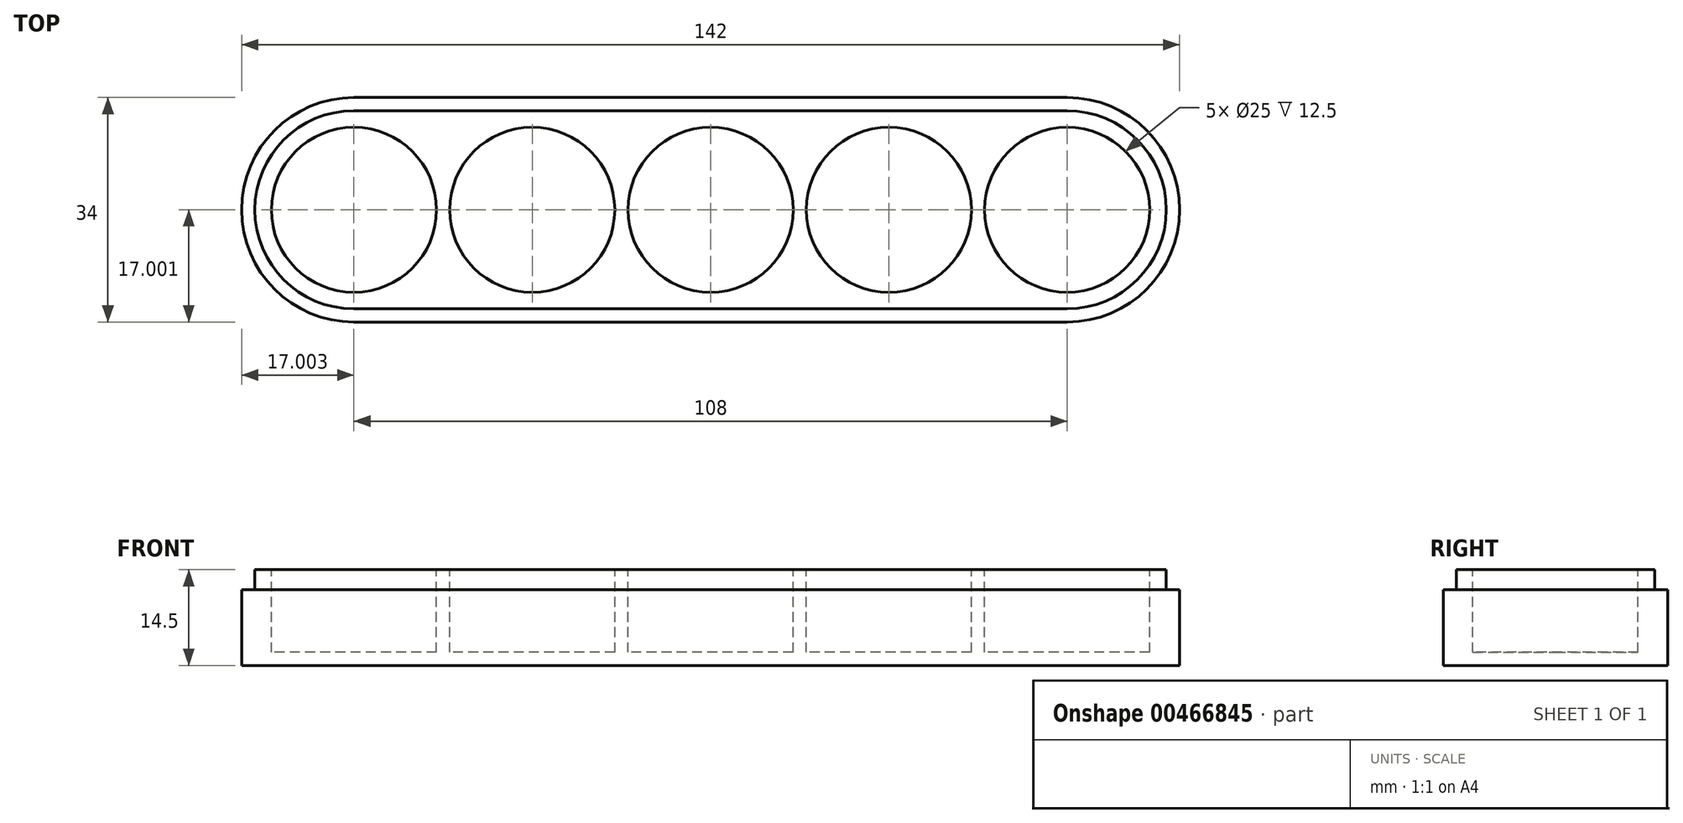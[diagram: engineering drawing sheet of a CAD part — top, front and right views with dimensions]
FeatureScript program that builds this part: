
annotation { "Feature Type Name" : "Feature", "Feature Type Description" : "" }
export const myFeature = defineFeature(function(context is Context, id is Id, definition is map)
    precondition{}
    {
        {
            var Q0;
            Q0=qCreatedBy(makeId("Top.planeOp"),FACE);
            var sketch = newSketch(context, id + "F0", { "sketchPlane" : qUnion([Q0])});
            skLineSegment(sketch, "E0.bottom", {"start": v(-55.97, 18.36) * mm, "end": v(52.03, 18.36) * mm});
            skLineSegment(sketch, "E0.top", {"start": v(-55.97, -15.64) * mm, "end": v(52.03, -15.64) * mm});
            skArc(sketch, "E1", {"start": v(-55.97, 18.36) * mm, "mid": v(-72.97, 1.36) * mm, "end": v(-55.97, -15.64) * mm});
            skArc(sketch, "E2", {"start": v(52.03, -15.64) * mm, "mid": v(69.03, 1.36) * mm, "end": v(52.03, 18.36) * mm});
            skSolve(sketch);
        }
        {
            var Q0;
            Q0=makeQuery(id+"F0.imprint","IMPRINT",FACE,{"disambiguationData":[TD([[makeQuery(id+"F0.imprint","IMPRINT",EDGE,{"derivedFrom":sQuery(id+"F0.wireOp",EDGE,"E0.bottom")}),-1.0]])]});
            extrude(context, id + "F1", {"entities" : qUnion([Q0]), "depth" : 11.5 * mm});
        }
        {
            var Q0;
            Q0=makeQuery(id+"F1.opExtrude","CAP_FACE",FACE,{"disambiguationData":[OSD([sQuery(id+"F0.wireOp",EDGE,"E0.bottom"),sQuery(id+"F0.wireOp",EDGE,"E0.top"),sQuery(id+"F0.wireOp",EDGE,"E1"),sQuery(id+"F0.wireOp",EDGE,"E2")])],"isStart":false});
            var sketch = newSketch(context, id + "F2", { "sketchPlane" : qUnion([Q0])});
            skArc(sketch, "E3.0.0", {"start": v(-55.97, 18.36) * mm, "mid": v(-72.97, 1.36) * mm, "end": v(-55.97, -15.64) * mm, "construction": true});
            skLineSegment(sketch, "E3.0.1", {"start": v(-55.97, -15.64) * mm, "end": v(52.03, -15.64) * mm, "construction": true});
            skArc(sketch, "E3.0.2", {"start": v(52.03, -15.64) * mm, "mid": v(69.03, 1.36) * mm, "end": v(52.03, 18.36) * mm, "construction": true});
            skLineSegment(sketch, "E3.0.3", {"start": v(52.03, 18.36) * mm, "end": v(-55.97, 18.36) * mm, "construction": true});
            skLineSegment(sketch, "E4.0", {"start": v(52.03, 16.36) * mm, "end": v(-55.97, 16.36) * mm});
            skArc(sketch, "E4.1", {"start": v(52.03, -13.64) * mm, "mid": v(67.03, 1.36) * mm, "end": v(52.03, 16.36) * mm});
            skLineSegment(sketch, "E4.2", {"start": v(-55.97, -13.64) * mm, "end": v(52.03, -13.64) * mm});
            skArc(sketch, "E4.3", {"start": v(-55.97, 16.36) * mm, "mid": v(-70.97, 1.36) * mm, "end": v(-55.97, -13.64) * mm});
            skSolve(sketch);
        }
        {
            var Q0;
            Q0=makeQuery(id+"F2.imprint","IMPRINT",FACE,{"disambiguationData":[TD([[makeQuery(id+"F2.imprint","IMPRINT",EDGE,{"derivedFrom":sQuery(id+"F2.wireOp",EDGE,"E4.0")}),1.0]])]});
            extrude(context, id + "F3", {"entities" : qUnion([Q0]), "operationType" : NewBodyOperationType.ADD, "depth" : 3 * mm});
        }
        {
            var Q0;
            Q0=makeQuery(id+"F3.opExtrude","CAP_FACE",FACE,{"disambiguationData":[OSD([sQuery(id+"F2.wireOp",EDGE,"E4.0"),sQuery(id+"F2.wireOp",EDGE,"E4.1"),sQuery(id+"F2.wireOp",EDGE,"E4.2"),sQuery(id+"F2.wireOp",EDGE,"E4.3")])],"isStart":false});
            var sketch = newSketch(context, id + "F4", { "sketchPlane" : qUnion([Q0])});
            skLineSegment(sketch, "E5", {"start": v(-55.97, 16.36) * mm, "end": v(-55.97, -13.64) * mm, "construction": true});
            skCircle(sketch, "E6", {"center": v(-55.97, 1.36) * mm, "radius": 12.5 * mm});
            skCircle(sketch, "E7.1.0.0", {"center": v(-28.97, 1.36) * mm, "radius": 12.5 * mm});
            skCircle(sketch, "E7.2.0.0", {"center": v(-1.97, 1.36) * mm, "radius": 12.5 * mm});
            skCircle(sketch, "E7.3.0.0", {"center": v(25.03, 1.36) * mm, "radius": 12.5 * mm});
            skCircle(sketch, "E7.4.0.0", {"center": v(52.03, 1.36) * mm, "radius": 12.5 * mm});
            skLineSegment(sketch, "E7.direction1", {"start": v(-55.97, 1.36) * mm, "end": v(-28.97, 1.36) * mm, "construction": true});
            skSolve(sketch);
        }
        {
            var Q0;
            Q0=makeQuery(id+"F4.imprint","IMPRINT",FACE,{"disambiguationData":[TD([[makeQuery(id+"F4.imprint","IMPRINT",EDGE,{"derivedFrom":sQuery(id+"F4.wireOp",EDGE,"E6")}),1.0]])]});
            var Q1;
            Q1=makeQuery(id+"F4.imprint","IMPRINT",FACE,{"disambiguationData":[TD([[makeQuery(id+"F4.imprint","IMPRINT",EDGE,{"derivedFrom":sQuery(id+"F4.wireOp",EDGE,"E7.1.0.0")}),1.0]])]});
            var Q2;
            Q2=makeQuery(id+"F4.imprint","IMPRINT",FACE,{"disambiguationData":[TD([[makeQuery(id+"F4.imprint","IMPRINT",EDGE,{"derivedFrom":sQuery(id+"F4.wireOp",EDGE,"E7.2.0.0")}),1.0]])]});
            var Q3;
            Q3=makeQuery(id+"F4.imprint","IMPRINT",FACE,{"disambiguationData":[TD([[makeQuery(id+"F4.imprint","IMPRINT",EDGE,{"derivedFrom":sQuery(id+"F4.wireOp",EDGE,"E7.3.0.0")}),1.0]])]});
            var Q4;
            Q4=makeQuery(id+"F4.imprint","IMPRINT",FACE,{"disambiguationData":[TD([[makeQuery(id+"F4.imprint","IMPRINT",EDGE,{"derivedFrom":sQuery(id+"F4.wireOp",EDGE,"E7.4.0.0")}),1.0]])]});
            extrude(context, id + "F5", {"entities" : qUnion([Q0, Q1, Q2, Q3, Q4]), "operationType" : NewBodyOperationType.REMOVE, "oppositeDirection" : true, "depth" : 12.5 * mm});
        }
    });
